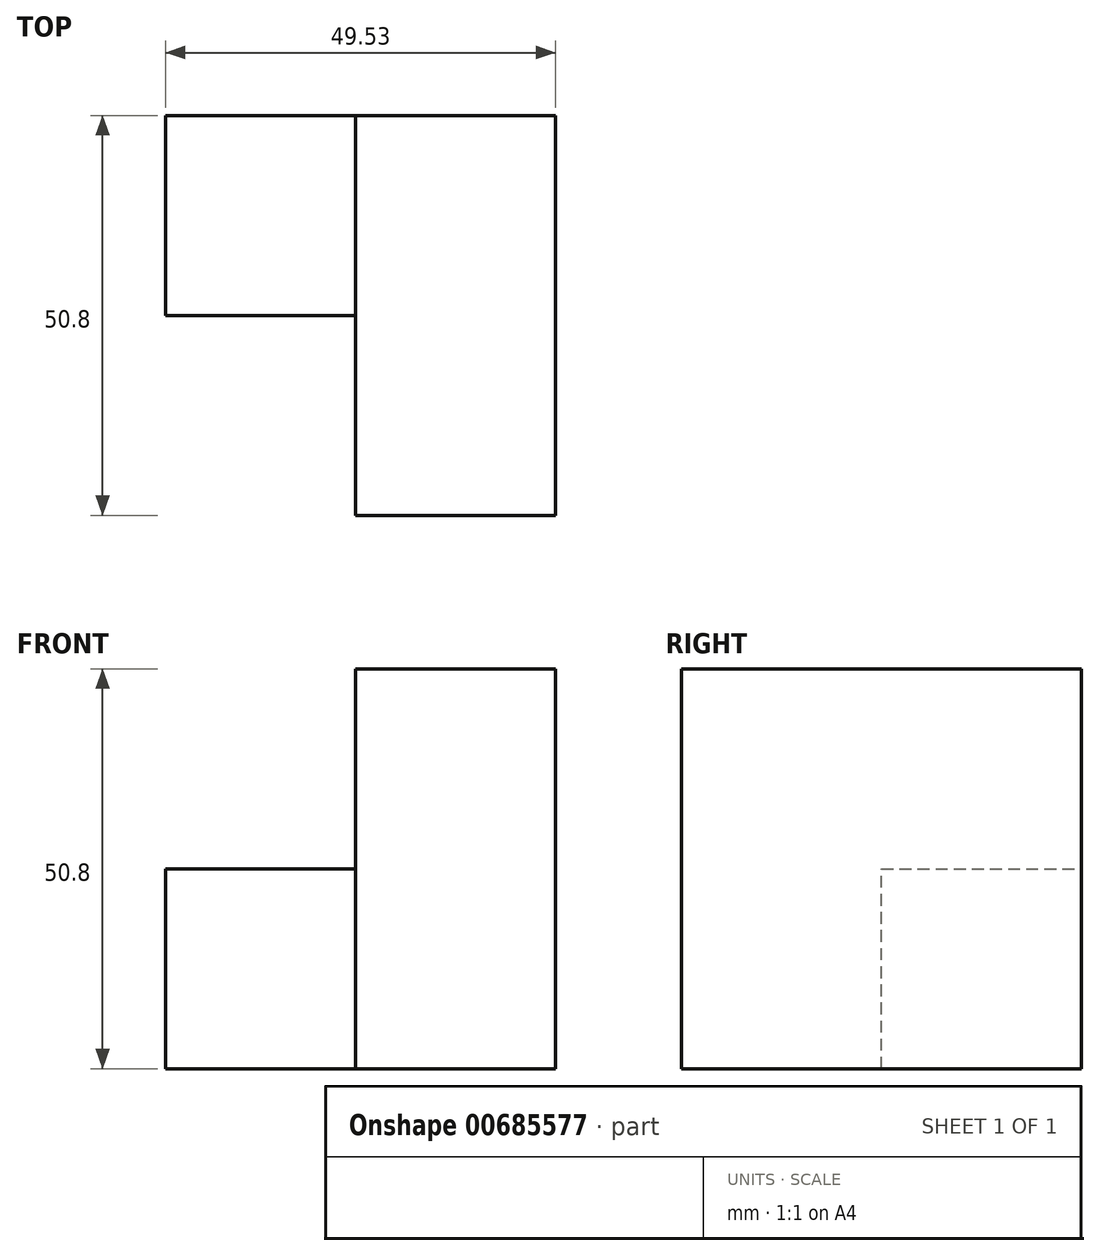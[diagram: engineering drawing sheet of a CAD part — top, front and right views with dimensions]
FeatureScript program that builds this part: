
annotation { "Feature Type Name" : "Feature", "Feature Type Description" : "" }
export const myFeature = defineFeature(function(context is Context, id is Id, definition is map)
    precondition{}
    {
        {
            var Q0;
            Q0=qCreatedBy(makeId("Front.planeOp"),FACE);
            var sketch = newSketch(context, id + "F0", { "sketchPlane" : qUnion([Q0])});
            skLineSegment(sketch, "E0", {"start": v(-31.57, 52.88) * mm, "end": v(-6.17, 52.88) * mm});
            skLineSegment(sketch, "E1", {"start": v(-6.17, 52.88) * mm, "end": v(-6.17, 2.08) * mm});
            skLineSegment(sketch, "E2", {"start": v(-6.17, 2.08) * mm, "end": v(-31.57, 2.08) * mm});
            skLineSegment(sketch, "E3", {"start": v(-31.57, 2.08) * mm, "end": v(-31.57, 52.88) * mm});
            skSolve(sketch);
        }
        {
            var Q0;
            Q0=qCreatedBy(makeId("Right.planeOp"),FACE);
            var sketch = newSketch(context, id + "F1", { "sketchPlane" : qUnion([Q0])});
            skLineSegment(sketch, "E4", {"start": v(0, 2.76) * mm, "end": v(0, 28.16) * mm});
            skLineSegment(sketch, "E5", {"start": v(0, 28.16) * mm, "end": v(-25.4, 28.16) * mm});
            skLineSegment(sketch, "E6", {"start": v(-25.4, 28.16) * mm, "end": v(-25.4, 2.76) * mm});
            skLineSegment(sketch, "E7", {"start": v(-25.4, 2.76) * mm, "end": v(0, 2.76) * mm});
            skSolve(sketch);
        }
        {
            var Q0;
            Q0=makeQuery(id+"F1.imprint","IMPRINT",FACE,{"disambiguationData":[TD([[makeQuery(id+"F1.imprint","IMPRINT",EDGE,{"derivedFrom":sQuery(id+"F1.wireOp",EDGE,"E4")}),1.0]])]});
            extrude(context, id + "F2", {"entities" : qUnion([Q0]), "depth" : 25.4 * mm, "offsetDistance" : 25.4 * mm});
        }
        {
            var Q0;
            Q0=makeQuery(id+"F0.imprint","IMPRINT",FACE,{"disambiguationData":[TD([[makeQuery(id+"F0.imprint","IMPRINT",EDGE,{"derivedFrom":sQuery(id+"F0.wireOp",EDGE,"E0")}),-1.0]])]});
            extrude(context, id + "F3", {"entities" : qUnion([Q0]), "depth" : 50.8 * mm, "offsetDistance" : 25.4 * mm});
        }
        {
            var Q0;
            Q0=makeQuery(id+"F3.opExtrude","SWEPT_BODY",BODY,{"disambiguationData":[OSD([sQuery(id+"F0.wireOp",EDGE,"E0"),sQuery(id+"F0.wireOp",EDGE,"E1"),sQuery(id+"F0.wireOp",EDGE,"E2"),sQuery(id+"F0.wireOp",EDGE,"E3")])]});
            var Q1;
            Q1=makeQuery(id+"F2.opExtrude","SWEPT_BODY",BODY,{"disambiguationData":[OSD([sQuery(id+"F1.wireOp",EDGE,"E4"),sQuery(id+"F1.wireOp",EDGE,"E5"),sQuery(id+"F1.wireOp",EDGE,"E6"),sQuery(id+"F1.wireOp",EDGE,"E7")])]});
            deleteBodies(context, id + "F4", {"entities" : qUnion([Q0, Q1])});
        }
        {
            var Q0;
            Q0=qCreatedBy(makeId("Front.planeOp"),FACE);
            var sketch = newSketch(context, id + "F5", { "sketchPlane" : qUnion([Q0])});
            skLineSegment(sketch, "E8", {"start": v(0, 0) * mm, "end": v(0, 50.8) * mm});
            skLineSegment(sketch, "E9", {"start": v(0, 50.8) * mm, "end": v(-25.4, 50.8) * mm});
            skLineSegment(sketch, "E10", {"start": v(-25.4, 50.8) * mm, "end": v(-25.4, 0) * mm});
            skLineSegment(sketch, "E11", {"start": v(-25.4, 0) * mm, "end": v(0, 0) * mm});
            skSolve(sketch);
        }
        {
            var Q0;
            Q0=qCreatedBy(makeId("Front.planeOp"),FACE);
            var sketch = newSketch(context, id + "F6", { "sketchPlane" : qUnion([Q0])});
            skLineSegment(sketch, "E12", {"start": v(-24.13, 0) * mm, "end": v(-49.53, 0) * mm});
            skLineSegment(sketch, "E13", {"start": v(-49.53, 0) * mm, "end": v(-49.53, 25.4) * mm});
            skLineSegment(sketch, "E14", {"start": v(-49.53, 25.4) * mm, "end": v(-23.68, 25.4) * mm});
            skLineSegment(sketch, "E15", {"start": v(-23.68, 25.4) * mm, "end": v(-24.13, 0) * mm});
            skSolve(sketch);
        }
        {
            var Q0;
            Q0 = qSketchRegion(id + "F6", true);
            extrude(context, id + "F7", {"entities" : qUnion([Q0]), "depth" : 25.4 * mm, "offsetDistance" : 25.4 * mm});
        }
        {
            var Q0;
            Q0=makeQuery(id+"F5.imprint","IMPRINT",FACE,{"disambiguationData":[TD([[makeQuery(id+"F5.imprint","IMPRINT",EDGE,{"derivedFrom":sQuery(id+"F5.wireOp",EDGE,"E8")}),1.0]])]});
            extrude(context, id + "F8", {"entities" : qUnion([Q0]), "operationType" : NewBodyOperationType.ADD, "depth" : 50.8 * mm, "offsetDistance" : 25.4 * mm});
        }
    });
